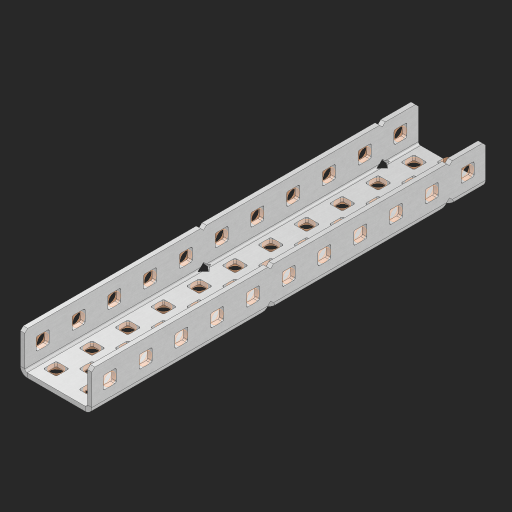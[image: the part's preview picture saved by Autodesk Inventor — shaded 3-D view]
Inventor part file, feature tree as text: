
AUTODESK INVENTOR PART (.ipt)
format: ipt  version: 2023 (Build 270158000, 158)  size: 998,400 bytes
history: native  units: in
note: dims shown in document units (in); Inventor stores cm internally (conversion verified against a paired STEP export)
features: other x62, extrude x53, sheet_metal_op x11, sketch x10, pattern_linear x2, mirror x1, chamfer x1
ambient origin geometry x8: Origin, YZ Plane, XZ Plane, XY Plane, X Axis, Y Axis, Z Axis, Center Point
bodies: Solid1 (feature_tree), Body (feature_tree)
feature tree (140):
  sheet_metal_op  "Flanges"
  other  "Flange Pattern Plane"
  other  "Flange Pattern Sketch"
  sheet_metal_op  "Flange Pattern"
  sheet_metal_op  "Body Pattern"
  pattern_linear  "Center Pattern"  Spacing1=0.0625in  [1 undecoded]
  other  "Arc Length"
  mirror  "Notch Mirror"
  pattern_linear  "Notch Pattern"  Spacing1=0.182in  [1 undecoded]
  chamfer  "End Chamfer"
  extrude  "Half Cut"  Depth=0.02in
  sketch  "Sketch1"  dims[d0=1.0in]
  other  "Plate1"
  sketch  "Sketch2"  dims[d1=5.5in]
  other  "Plate2"
  sheet_metal_op  "Bend1"
  sheet_metal_op  "Corner1"
  sketch  "Sketch3"  dims[d2=0.0625in]
  sketch  "Sketch7"  dims[d3=0.0625in]
  other  "Srf1"
  other  "Srf2"
  sketch  "Sketch8"  dims[d4=0.0312in]
  sketch  "Sketch9"  dims[d5=0.125in]
  other  "Srf91"
  sheet_metal_op  "Body Pattern Sketch"
  other  "Srf92"
  sketch  "Sketch13"  dims[d6=0.0625in]
  sketch  "Sketch14"  dims[d7=0.5in d8=90.0deg d9=0.0312in]
  sketch  "Sketch15"  dims[d10=0.25in]
  sketch  "Sketch16"  dims[d11=0.0625in d12=0.0625in d16=0.182in d17=0.02in d18=0.0625in d19=0.0in d20=0.25in d21=0.25in d38=4.3307in d40=0.5in d41=0.7874in d43=1.0in d46=0.172in d47=1.0in d48=0.0in d49=0.182in d50=0.02in d51=0.25in d52=0.25in d53=0.0625in d54=0.0in d55=0.172in d56=1.0in d57=0.0in d58=0.25in d60=4.3307in d62=0.5in d63=0.7874in d65=0.5in d85=0.1473in d86=0.1782in d88=0.04in d89=0.0625in d90=0.0in d91=0.04in d92=0.0491in d95=2.5in d96=0.04in d97=0.25in d98=45.0deg d99=0.25in d100=0.5in d101=0.0in d102=2.497in d106=0.182in d107=0.02in d108=0.5in d109=0.5in d110=0.0625in d111=0.0in d112=0.172in d113=0.5in d114=0.0in d117=0.5in d118=0.5in d119=0.5in]
  other  "Srf786"
  other  "Srf823"
  other  "Srf824"
  other  "Srf825"
  other  "Srf826"
  other  "Srf827"
  other  "Srf828"
  other  "Srf829"
  other  "Srf856"
  other  "Srf857"
  other  "Srf858"
  other  "Srf859"
  other  "Srf860"
  other  "Srf861"
  other  "Srf862"
  other  "Srf889"
  other  "Srf890"
  other  "Srf891"
  other  "Srf892"
  other  "Srf893"
  other  "Srf894"
  other  "Srf895"
  other  "Srf896"
  other  "Srf922"
  other  "Srf923"
  other  "Srf924"
  other  "Srf925"
  other  "Srf926"
  other  "Srf959"
  other  "Srf960"
  other  "Srf961"
  other  "Srf962"
  other  "Srf963"
  other  "Srf996"
  other  "Srf997"
  other  "Srf1143"
  other  "Srf1144"
  other  "Srf1145"
  other  "Srf1146"
  other  "Srf1147"
  other  "Srf1148"
  other  "Srf1149"
  other  "Srf1150"
  other  "Srf1199"
  other  "Srf1200"
  other  "Srf1201"
  other  "Srf1202"
  other  "Srf1203"
  other  "Srf1204"
  other  "Srf1205"
  other  "Srf1206"
  sheet_metal_op  "Flange Stamp"
  sheet_metal_op  "Flange Circle"
  sheet_metal_op  "Body Stamp"
  sheet_metal_op  "Body Circle"
  other  "Center Stamp"
  other  "Center Circle"
  sheet_metal_op  "Notch"
  extrude  "ExtrusionSrf2"  Depth=0.0625in
  extrude  "ExtrusionSrf92"  TaperAngle=0.0deg  [1 undecoded]
  extrude  "ExtrusionSrf823"  Depth=0.5in
  extrude  "ExtrusionSrf824"  Depth=0.5in
  extrude  "ExtrusionSrf825"  Depth=0.5in
  extrude  "ExtrusionSrf826"  Depth=0.5in
  extrude  "ExtrusionSrf827"  Depth=1.0in TaperAngle=0.0deg
  extrude  "ExtrusionSrf828"  Depth=0.5in
  extrude  "ExtrusionSrf829"  Depth=0.02in
  extrude  "ExtrusionSrf856"  Depth=0.5in
  extrude  "ExtrusionSrf857"  Depth=0.5in
  extrude  "ExtrusionSrf858"  Depth=0.0625in
  extrude  "ExtrusionSrf859"  TaperAngle=0.0deg  [1 undecoded]
  extrude  "ExtrusionSrf860"  Depth=0.5in
  extrude  "ExtrusionSrf861"  Depth=1.0in TaperAngle=0.0deg
  extrude  "ExtrusionSrf862"  Depth=0.5in
  extrude  "ExtrusionSrf889"  Depth=0.5in
  extrude  "ExtrusionSrf890"  Depth=0.5in
  extrude  "ExtrusionSrf891"  Depth=0.5in
  extrude  "ExtrusionSrf892"  Depth=0.5in
  extrude  "ExtrusionSrf893"  Depth=0.5in
  extrude  "ExtrusionSrf894"  Depth=0.0625in
  extrude  "ExtrusionSrf895"  TaperAngle=0.0deg  [1 undecoded]
  extrude  "ExtrusionSrf896"  Depth=0.5in
  extrude  "ExtrusionSrf922"  Depth=0.5in
  extrude  "ExtrusionSrf923"  Depth=2.5in
  extrude  "ExtrusionSrf924"  Depth=0.5in TaperAngle=45.0deg
  extrude  "ExtrusionSrf925"  Depth=0.5in
  extrude  "ExtrusionSrf926"  Depth=0.5in TaperAngle=0.0deg
  extrude  "ExtrusionSrf959"  Depth=0.5in
  extrude  "ExtrusionSrf960"  Depth=0.5in
  extrude  "ExtrusionSrf961"  Depth=0.02in
  extrude  "ExtrusionSrf962"  Depth=0.5in
  extrude  "ExtrusionSrf963"  Depth=0.5in
  extrude  "ExtrusionSrf996"  Depth=0.0625in
  extrude  "ExtrusionSrf997"  TaperAngle=0.0deg  [1 undecoded]
  extrude  "ExtrusionSrf1143"  Depth=0.5in
  extrude  "ExtrusionSrf1144"  Depth=0.5in TaperAngle=0.0deg
  extrude  "ExtrusionSrf1145"  Depth=0.5in
  extrude  "ExtrusionSrf1146"  Depth=0.5in
  extrude  "ExtrusionSrf1147"  Depth=0.5in
  extrude  "ExtrusionSrf1148"  [1 undecoded]
  extrude  "ExtrusionSrf1149"  [1 undecoded]
  extrude  "ExtrusionSrf1150"  [1 undecoded]
  extrude  "ExtrusionSrf1199"  [1 undecoded]
  extrude  "ExtrusionSrf1200"  [1 undecoded]
  extrude  "ExtrusionSrf1201"  [1 undecoded]
  extrude  "ExtrusionSrf1202"  [1 undecoded]
  extrude  "ExtrusionSrf1203"  [1 undecoded]
  extrude  "ExtrusionSrf1204"  [1 undecoded]
  extrude  "ExtrusionSrf1205"  [1 undecoded]
  extrude  "ExtrusionSrf1206"  [1 undecoded]
note: 17 required parameter values undecoded (feature->parameter linkage not recoverable at this tier; creation-order binding heuristic only, values carry confidence <= 0.55)
